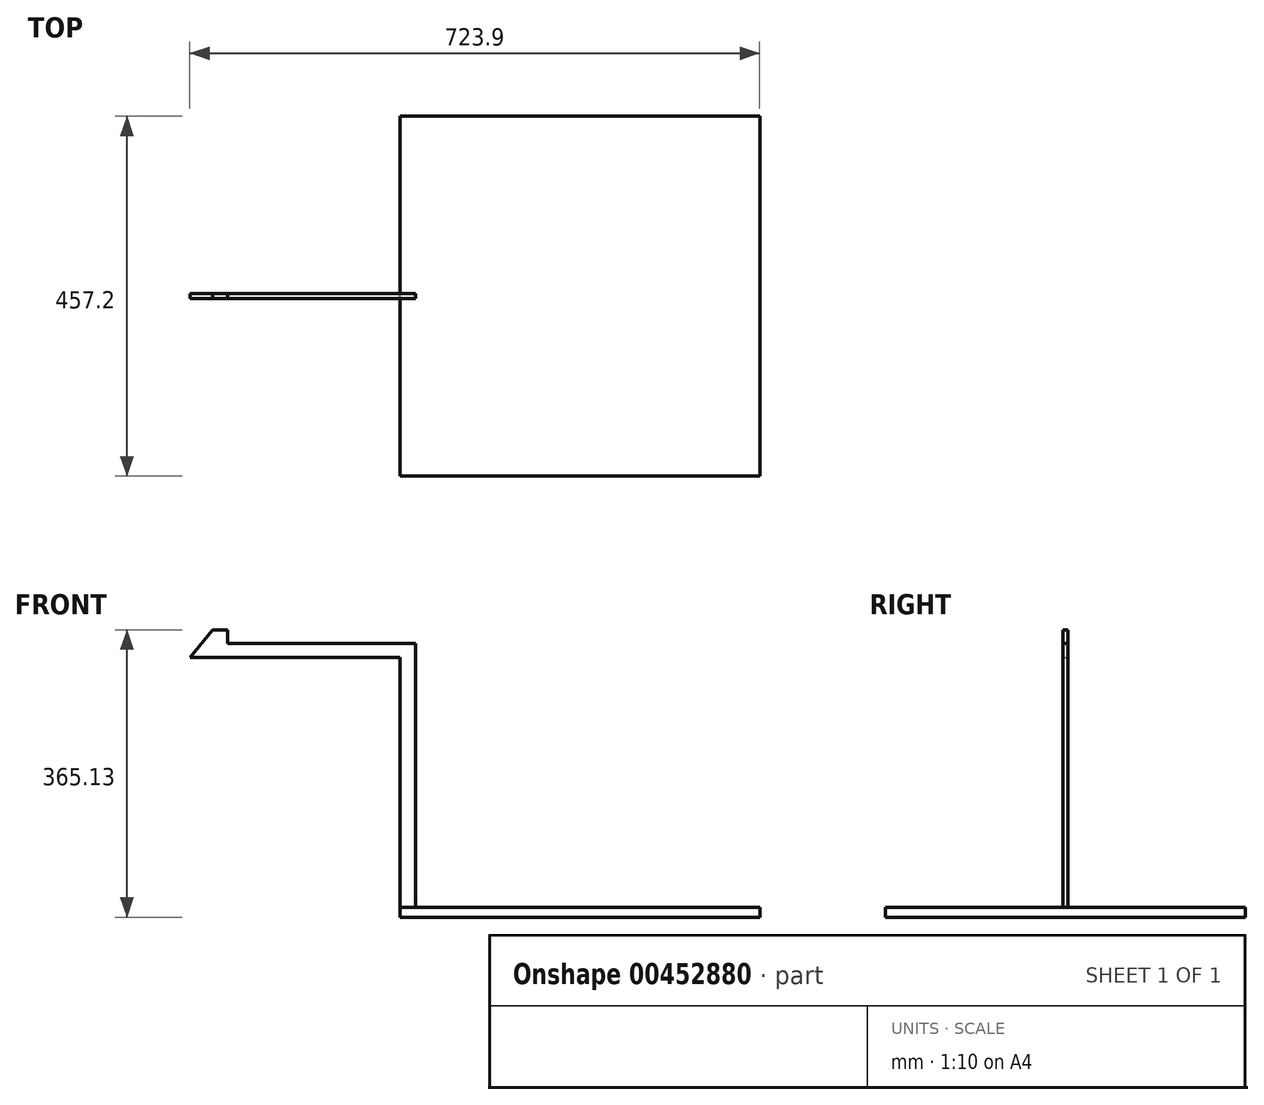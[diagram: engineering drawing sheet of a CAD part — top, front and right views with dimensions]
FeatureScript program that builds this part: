
annotation { "Feature Type Name" : "Feature", "Feature Type Description" : "" }
export const myFeature = defineFeature(function(context is Context, id is Id, definition is map)
    precondition{}
    {
        {
            var Q0;
            Q0=qCreatedBy(makeId("Front.planeOp"),FACE);
            var sketch = newSketch(context, id + "F0", { "sketchPlane" : qUnion([Q0])});
            skLineSegment(sketch, "E0", {"start": v(-31.1, 0) * mm, "end": v(597.55, 0) * mm});
            skLineSegment(sketch, "E1", {"start": v(597.55, 0) * mm, "end": v(597.55, 330.2) * mm});
            skLineSegment(sketch, "E2", {"start": v(378.9, 365.13) * mm, "end": v(360.1, 365.13) * mm});
            skLineSegment(sketch, "E3", {"start": v(330.85, 330.2) * mm, "end": v(597.55, 330.2) * mm});
            skLineSegment(sketch, "E4", {"start": v(-31.1, 0) * mm, "end": v(-31.1, 79.38) * mm});
            skLineSegment(sketch, "E5", {"start": v(76.95, 158.75) * mm, "end": v(597.55, 158.75) * mm});
            skLineSegment(sketch, "E6", {"start": v(330.85, 330.2) * mm, "end": v(360.1, 365.13) * mm});
            skLineSegment(sketch, "E7", {"start": v(360.1, 365.13) * mm, "end": v(378.9, 365.13) * mm});
            skLineSegment(sketch, "E8", {"start": v(597.55, 330.2) * mm, "end": v(597.55, 347.66) * mm});
            skLineSegment(sketch, "E9", {"start": v(597.55, 347.66) * mm, "end": v(378.9, 347.66) * mm});
            skLineSegment(sketch, "E10", {"start": v(378.9, 347.66) * mm, "end": v(378.9, 365.13) * mm});
            skPoint(sketch, "E11.orphan", {"position": v(597.55, 365.13) * mm});
            skArc(sketch, "E12", {"start": v(76.95, 158.75) * mm, "mid": v(10.85, 135.5) * mm, "end": v(-31.1, 79.38) * mm});
            skPoint(sketch, "E13.orphan", {"position": v(-31.1, 158.75) * mm});
            skLineSegment(sketch, "E14.0", {"start": v(617.55, 330.2) * mm, "end": v(617.55, 347.66) * mm});
            skLineSegment(sketch, "E14.1", {"start": v(617.55, 0) * mm, "end": v(617.55, 330.2) * mm});
            skLineSegment(sketch, "E15", {"start": v(597.55, 347.66) * mm, "end": v(617.55, 347.66) * mm});
            skLineSegment(sketch, "E16", {"start": v(617.55, 0) * mm, "end": v(597.55, 0) * mm});
            skSolve(sketch);
        }
        {
            var Q0;
            Q0 = qSketchRegion(id + "F0", true);
            extrude(context, id + "F1", {"entities" : qUnion([Q0]), "depth" : 6.35 * mm});
        }
        {
            var Q0;
            {var subQ1=sQuery(id+"F0.wireOp",EDGE,"E0");Q0=makeQuery(id+"F0.imprint","IMPRINT",FACE,{"disambiguationData":[TD([[makeQuery(id+"F0.imprint","IMPRINT",EDGE,{"derivedFrom":subQ1}),1.0]])]});}
            extrude(context, id + "F2", {"entities" : qUnion([Q0]), "operationType" : NewBodyOperationType.REMOVE, "depth" : 25 * mm});
        }
        {
            var Q0;
            Q0=makeQuery(id+"F1.opExtrude","SWEPT_FACE",FACE,{"disambiguationData":[OSD([sQuery(id+"F0.wireOp",EDGE,"E0"),sQuery(id+"F0.wireOp",EDGE,"E16")])]});
            var sketch = newSketch(context, id + "F3", { "sketchPlane" : qUnion([Q0])});
            skLineSegment(sketch, "E17", {"start": v(597.55, 3.18) * mm, "end": v(597.55, -225.43) * mm});
            skLineSegment(sketch, "E18", {"start": v(597.55, 3.18) * mm, "end": v(597.55, 16.7) * mm});
            skLineSegment(sketch, "E19.bottom", {"start": v(597.55, -225.43) * mm, "end": v(1054.75, -225.43) * mm});
            skLineSegment(sketch, "E19.top", {"start": v(597.55, 231.78) * mm, "end": v(1054.75, 231.78) * mm});
            skLineSegment(sketch, "E19.left", {"start": v(597.55, -225.43) * mm, "end": v(597.55, 231.78) * mm});
            skLineSegment(sketch, "E19.right", {"start": v(1054.75, -225.42) * mm, "end": v(1054.75, 231.78) * mm});
            skSolve(sketch);
        }
        {
            var Q0;
            Q0 = qSketchRegion(id + "F3", true);
            extrude(context, id + "F4", {"entities" : qUnion([Q0]), "operationType" : NewBodyOperationType.ADD, "oppositeDirection" : true, "depth" : 12.7 * mm});
        }
    });
